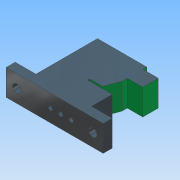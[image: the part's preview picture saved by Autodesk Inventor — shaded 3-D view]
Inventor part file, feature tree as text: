
AUTODESK INVENTOR PART (.ipt)
format: ipt  version: 2012 SP1 (Build 160190100, 190)  size: 125,440 bytes
history: native  units: mm
features: sketch x3, hole x2, extrude x1
ambient origin geometry x8: Origin, YZ Plane, XZ Plane, XY Plane, X Axis, Y Axis, Z Axis, Center Point
bodies: Volumenkörper1 (feature_tree)
feature tree (6):
  extrude  "Extrusion1"  Depth=3.5mm
  hole  "Bohrung1"  [1 undecoded]
  hole  "Bohrung2"  [1 undecoded]
  sketch  "Skizze1"  dims[d0=27.3mm d1=3.5mm]
  sketch  "Skizze2"  dims[d2=37.5mm d3=8.0mm]
  sketch  "Skizze3"  dims[d4=19.0mm d5=6.0mm d6=6.0mm d7=15.0mm d8=11.5mm d9=21.5mm d10=12.0mm d11=17.0mm d12=2.0mm d13=12.217305mm d14=10.0mm d15=0.0mm d16=16.5mm d17=4.0mm d18=4.0mm d19=5.0mm d20=5.0mm d21=5.0mm d22=1.8mm d23=6.0mm d24=4.0mm d25=2.0mm d26=90.0deg d27=3.0mm d28=20.594885mm d30=12.5mm d31=17.0mm d32=5.0mm d33=5.0mm d34=3.2mm d35=6.0mm d36=6.5mm d37=3.4mm d38=90.0deg d39=3.5mm d40=20.594885mm]
note: 2 required parameter values undecoded (feature->parameter linkage not recoverable at this tier; creation-order binding heuristic only, values carry confidence <= 0.55)
